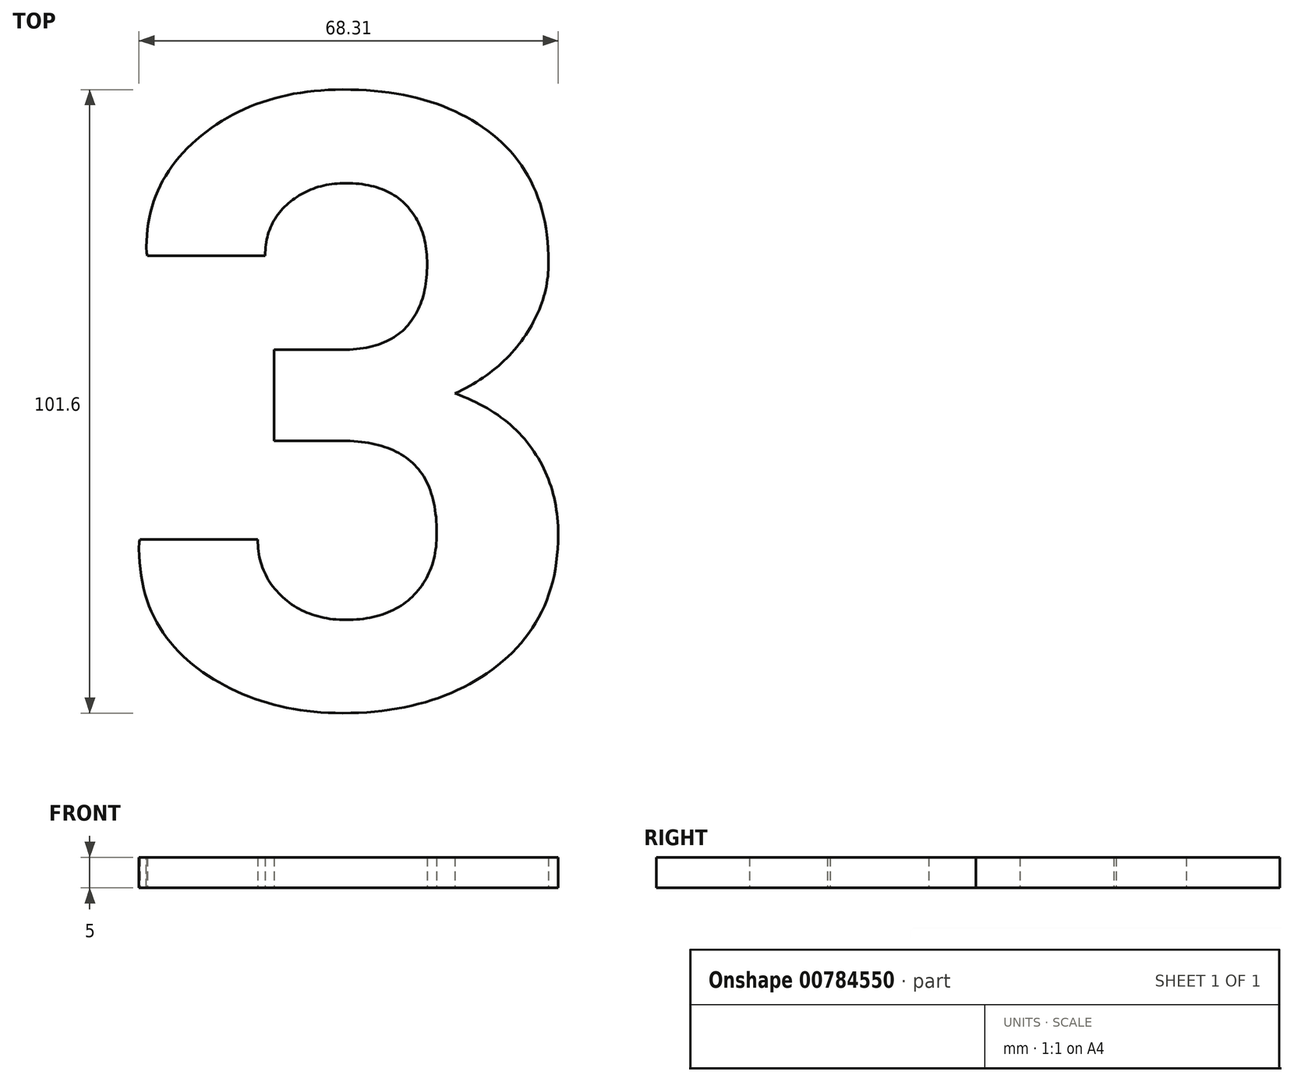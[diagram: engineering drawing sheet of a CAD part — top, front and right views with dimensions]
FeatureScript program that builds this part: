
annotation { "Feature Type Name" : "Feature", "Feature Type Description" : "" }
export const myFeature = defineFeature(function(context is Context, id is Id, definition is map)
    precondition{}
    {
        {
            var Q0;
            Q0=qCreatedBy(makeId("Top.planeOp"),FACE);
            var sketch = newSketch(context, id + "F0", { "sketchPlane" : qUnion([Q0])});
            skText(sketch, "E0", { "text": "3", "fontName": "RobotoSlab-Bold.ttf"});
            const initialGuessF0  = {"E0": [0, 0, 1, 0, 0.1]};
            skSetInitialGuess(sketch, initialGuessF0);
            skSolve(sketch);
        }
        {
            var Q0;
            Q0 = qSketchRegion(id + "F0", true);
            extrude(context, id + "F1", {"entities" : qUnion([Q0]), "depth" : 5 * mm, "offsetDistance" : 25 * mm});
        }
    });
